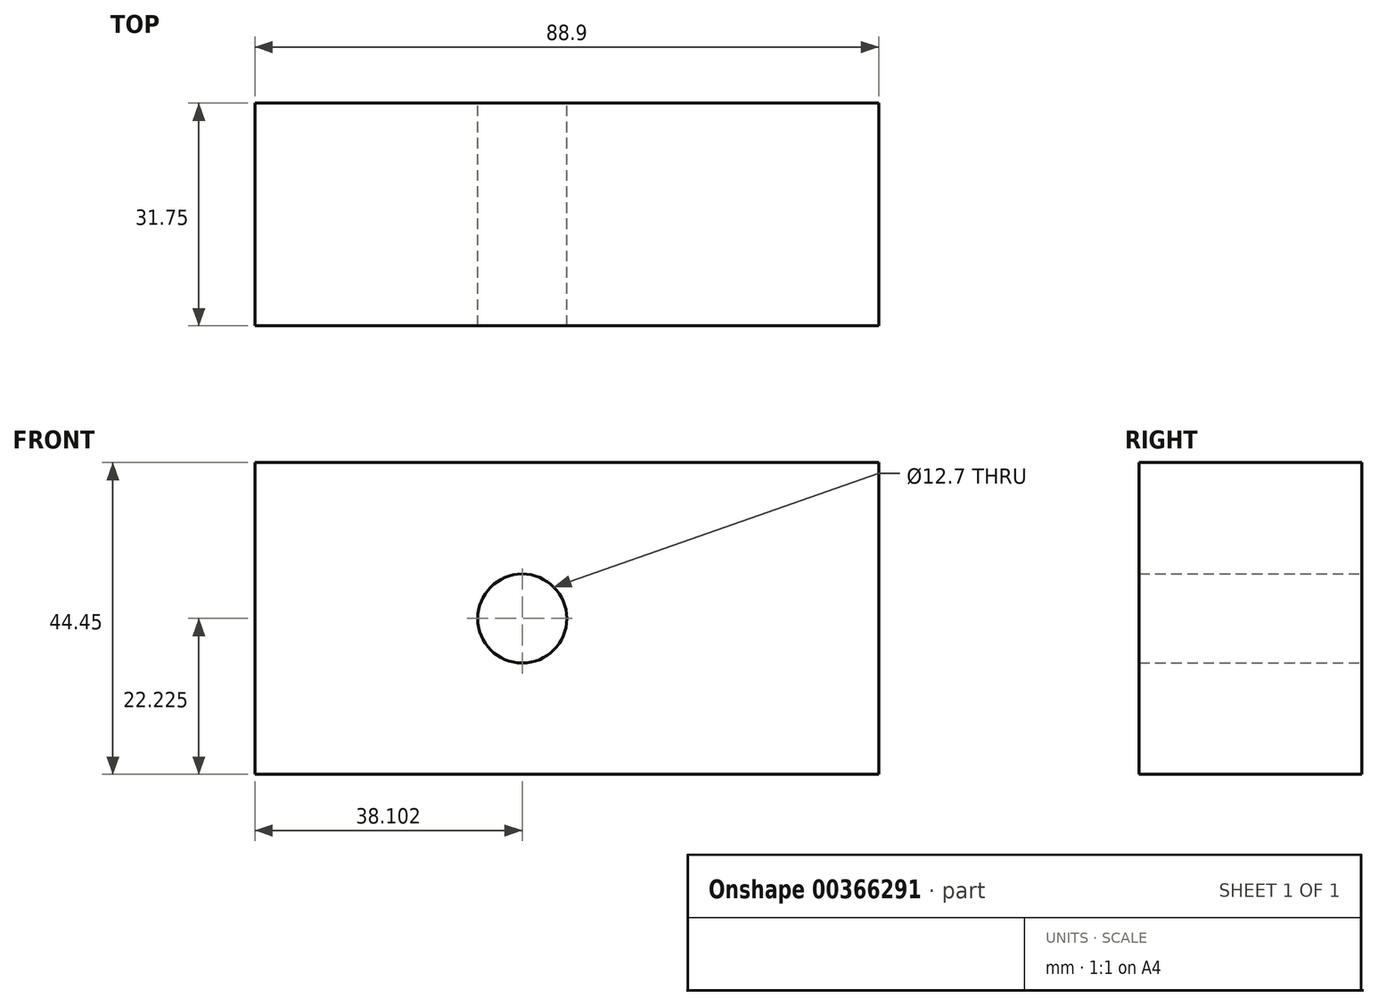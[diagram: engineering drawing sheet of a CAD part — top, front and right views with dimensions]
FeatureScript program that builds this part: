
annotation { "Feature Type Name" : "Feature", "Feature Type Description" : "" }
export const myFeature = defineFeature(function(context is Context, id is Id, definition is map)
    precondition{}
    {
        {
            var Q0;
            Q0=qCreatedBy(makeId("Front.planeOp"),FACE);
            var sketch = newSketch(context, id + "F0", { "sketchPlane" : qUnion([Q0])});
            skLineSegment(sketch, "E0", {"start": v(-47.89, 44.45) * mm, "end": v(41.01, 44.45) * mm});
            skLineSegment(sketch, "E1", {"start": v(41.01, 44.45) * mm, "end": v(41.01, 0) * mm});
            skLineSegment(sketch, "E2", {"start": v(41.01, 0) * mm, "end": v(-47.89, 0) * mm});
            skLineSegment(sketch, "E3", {"start": v(-47.89, 0) * mm, "end": v(-47.89, 44.45) * mm});
            skCircle(sketch, "E4", {"center": v(-9.79, 22.22) * mm, "radius": 6.35 * mm});
            skSolve(sketch);
        }
        {
            var Q0;
            Q0 = qSketchRegion(id + "F0", true);
            extrude(context, id + "F1", {"entities" : qUnion([Q0]), "depth" : 31.75 * mm});
        }
    });
